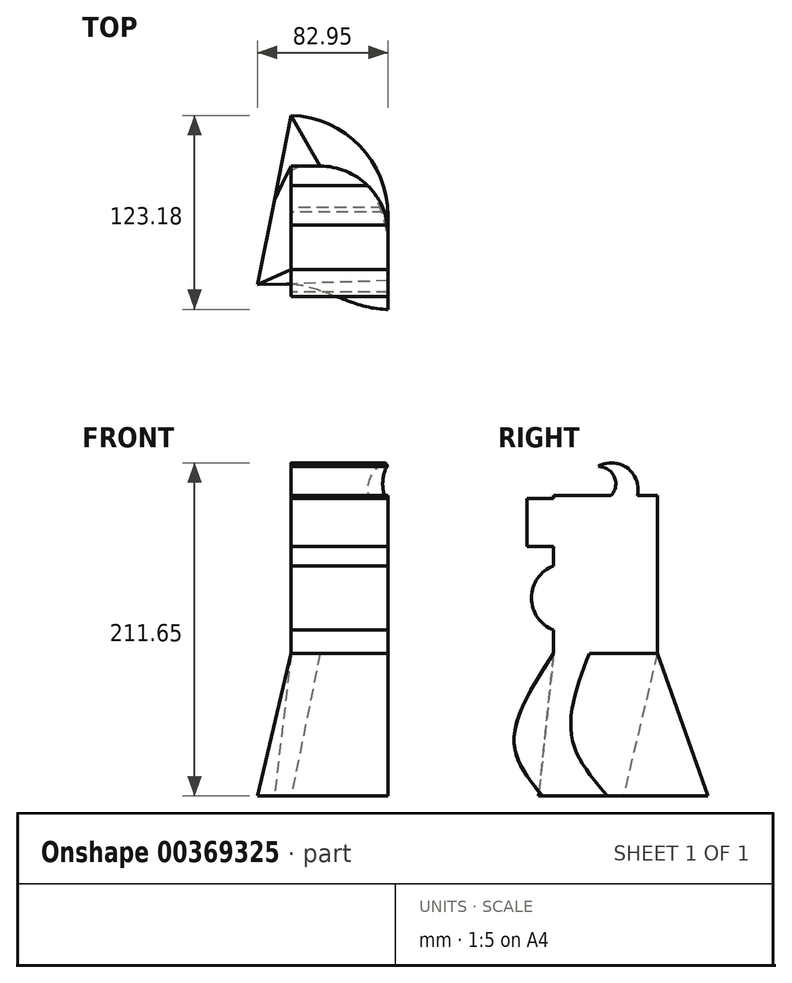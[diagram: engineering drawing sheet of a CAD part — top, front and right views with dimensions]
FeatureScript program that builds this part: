
annotation { "Feature Type Name" : "Feature", "Feature Type Description" : "" }
export const myFeature = defineFeature(function(context is Context, id is Id, definition is map)
    precondition{}
    {
        {
            var Q0;
            Q0=qCreatedBy(makeId("Right.planeOp"),FACE);
            var sketch = newSketch(context, id + "F0", { "sketchPlane" : qUnion([Q0])});
            skLineSegment(sketch, "E0.bottom", {"start": v(18.96, 41) * mm, "end": v(-46.9, 41) * mm});
            skLineSegment(sketch, "E0.top", {"start": v(18.96, -59.33) * mm, "end": v(-46.9, -59.33) * mm});
            skLineSegment(sketch, "E0.left", {"start": v(18.96, 41) * mm, "end": v(18.96, -59.33) * mm});
            skLineSegment(sketch, "E0.right", {"start": v(-46.9, 41) * mm, "end": v(-46.9, -59.33) * mm});
            skArc(sketch, "E1", {"start": v(-26.4, 41) * mm, "mid": v(5.34, 38.32) * mm, "end": v(-18.6, 59.33) * mm});
            skArc(sketch, "E2", {"start": v(-26.4, 41) * mm, "mid": v(-8.33, 44.14) * mm, "end": v(-18.6, 59.33) * mm});
            skArc(sketch, "E3", {"start": v(22.4, 8.53) * mm, "mid": v(5.33, -20.45) * mm, "end": v(35.3, -35.75) * mm});
            skCircle(sketch, "E4", {"center": v(-39.28, -24.13) * mm, "radius": 21.74 * mm});
            skLineSegment(sketch, "E5.bottom", {"start": v(-34.2, 8.53) * mm, "end": v(-63.78, 8.53) * mm});
            skLineSegment(sketch, "E5.top", {"start": v(-34.2, 39.01) * mm, "end": v(-63.78, 39.01) * mm});
            skLineSegment(sketch, "E5.left", {"start": v(-34.2, 8.53) * mm, "end": v(-34.2, 39.01) * mm});
            skLineSegment(sketch, "E5.right", {"start": v(-63.78, 8.53) * mm, "end": v(-63.78, 39.01) * mm});
            skSolve(sketch);
        }
        {
            var Q0;
            Q0 = qSketchRegion(id + "F0", true);
            extrude(context, id + "F1", {"entities" : qUnion([Q0]), "depth" : 61.5 * mm});
        }
        {
            var Q0;
            Q0=makeQuery(id+"F1.opExtrude","CAP_EDGE",EDGE,{"disambiguationData":[OSD([sQuery(id+"F0.wireOp",EDGE,"E0.left")])],"isStart":false});
            fillet(context, id + "F2", {"entities" : qUnion([Q0]), "radius" : 43.2 * mm, "tangentPropagation" : true, "allowEdgeOverflow" : false});
        }
        {
            var Q0;
            Q0=qCreatedBy(makeId("Top.planeOp"),FACE);
            cPlane(context, id + "F3", {"entities" : qUnion([Q0]), "cplaneType" : CPlaneType.OFFSET, "offset" : 150 * mm, "oppositeDirection" : true, "width" : 150 * mm, "height" : 150 * mm});
        }
        {
            var Q0;
            Q0=qCreatedBy(id+"F3.planeOp",FACE);
            var sketch = newSketch(context, id + "F4", { "sketchPlane" : qUnion([Q0])});
            skLineSegment(sketch, "E6", {"start": v(61.5, -53.9) * mm, "end": v(61.5, -12.58) * mm});
            skArc(sketch, "E7", {"start": v(61.5, -12.58) * mm, "mid": v(43.62, 31.7) * mm, "end": v(0, 51.11) * mm});
            skLineSegment(sketch, "E8", {"start": v(61.5, -53.9) * mm, "end": v(-21.45, -56.4) * mm});
            skLineSegment(sketch, "E9", {"start": v(-21.45, -56.4) * mm, "end": v(0, 51.11) * mm});
            skLineSegment(sketch, "E10.0", {"start": v(61.5, -24.25) * mm, "end": v(61.5, -46.9) * mm, "construction": true});
            skSolve(sketch);
        }
        {
            var Q0;
            Q0=makeQuery(id+"F1.opExtrude","CAP_FACE",FACE,{"disambiguationData":[OSD([sQuery(id+"F0.wireOp",EDGE,"E0.bottom"),sQuery(id+"F0.wireOp",EDGE,"E0.top"),sQuery(id+"F0.wireOp",EDGE,"E0.left"),sQuery(id+"F0.wireOp",EDGE,"E0.right"),sQuery(id+"F0.wireOp",EDGE,"E1"),sQuery(id+"F0.wireOp",EDGE,"E2"),sQuery(id+"F0.wireOp",EDGE,"E4"),sQuery(id+"F0.wireOp",EDGE,"E5.bottom"),sQuery(id+"F0.wireOp",EDGE,"E5.top"),sQuery(id+"F0.wireOp",EDGE,"E5.right")])],"isStart":false});
            var sketch = newSketch(context, id + "F5", { "sketchPlane" : qUnion([Q0])});
            skPoint(sketch, "E11.0", {"position": v(-53.9, -150) * mm});
            skPoint(sketch, "E12.0", {"position": v(-46.9, -59.33) * mm});
            skFitSpline(sketch, "E13", {"points": [v(-53.9, -150) * mm, v(-72.05, -115.16) * mm, v(-46.9, -59.33) * mm], "startDerivative": vector(-59.95, 73.4) * mm, "endDerivative": vector(69.19, 106.71) * mm});
            skSolve(sketch);
        }
        {
            var Q1;
            Q1=makeQuery(id+"F1.opExtrude","SWEPT_FACE",FACE,{"disambiguationData":[OSD([sQuery(id+"F0.wireOp",EDGE,"E0.top")])]});
            var Q2;
            Q2=makeQuery(id+"F4.imprint","IMPRINT",FACE,{"disambiguationData":[TD([[makeQuery(id+"F4.imprint","IMPRINT",EDGE,{"derivedFrom":sQuery(id+"F4.wireOp",EDGE,"E6")}),1.0]])]});
            var Q3;
            Q3=sQuery(id+"F5.wireOp",EDGE,"E13");
            loft(context, id + "F6", {"operationType" : NewBodyOperationType.ADD, "addGuides" : true, "sheetProfilesArray" : [{ "sheetProfileEntities" : qUnion([Q1]) }, { "sheetProfileEntities" : qUnion([Q2]) }], "guidesArray" : [{ "guideEntities" : qUnion([Q3]), "guideDerivativeType" : LoftGuideDerivativeType.DEFAULT, "guideDerivativeMagnitude" : 1 }]});
        }
    });
